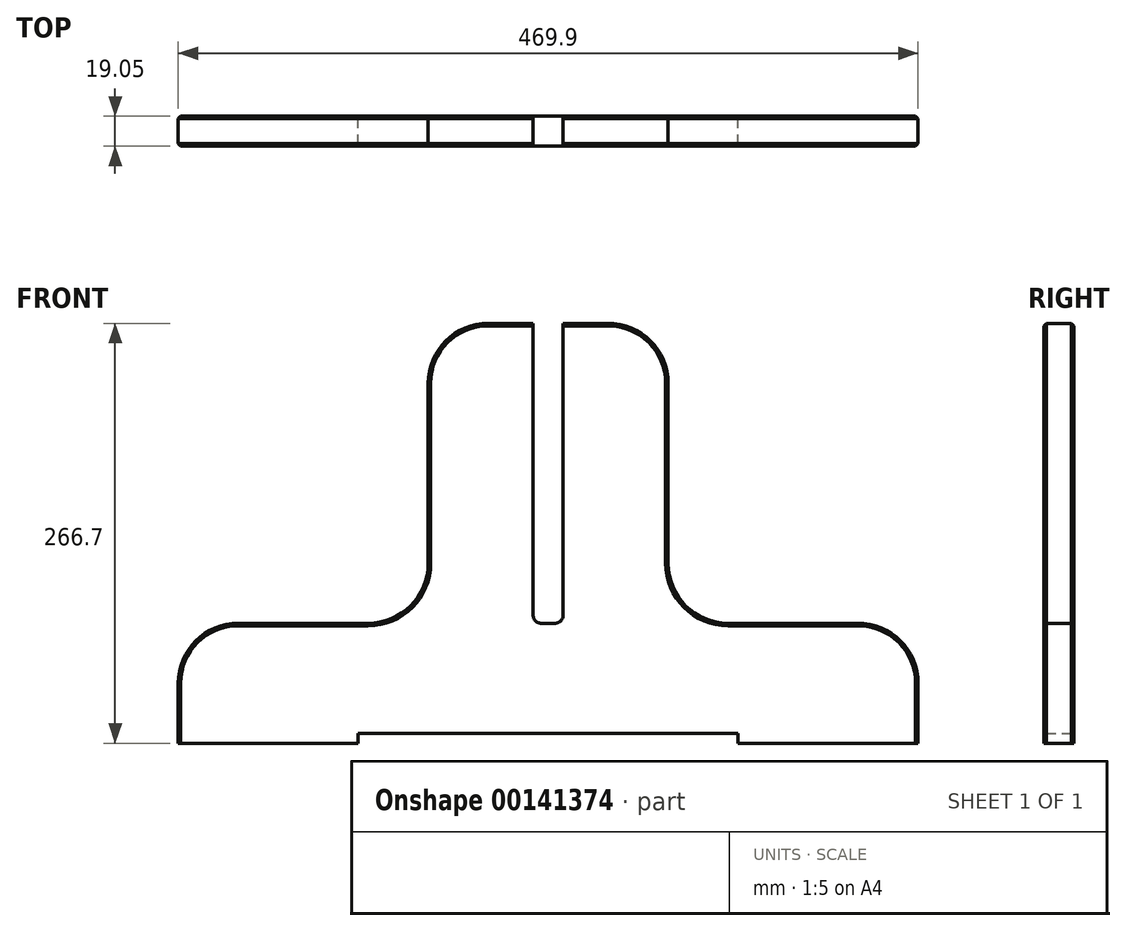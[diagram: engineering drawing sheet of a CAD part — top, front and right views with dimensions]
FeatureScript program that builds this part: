
annotation { "Feature Type Name" : "Feature", "Feature Type Description" : "" }
export const myFeature = defineFeature(function(context is Context, id is Id, definition is map)
    precondition{}
    {
        {
            var Q0;
            Q0=qCreatedBy(makeId("Front.planeOp"),FACE);
            var sketch = newSketch(context, id + "F0", { "sketchPlane" : qUnion([Q0])});
            skLineSegment(sketch, "E0.left", {"start": v(76.2, 95.25) * mm, "end": v(76.2, -95.25) * mm});
            skLineSegment(sketch, "E0.right", {"start": v(-76.2, 95.25) * mm, "end": v(-76.2, -95.25) * mm});
            skPoint(sketch, "E0.middle", {"position": v(0, 0) * mm});
            skLineSegment(sketch, "E1", {"start": v(-234.95, -171.45) * mm, "end": v(-234.95, -95.25) * mm});
            skLineSegment(sketch, "E2", {"start": v(-234.95, -95.25) * mm, "end": v(-76.2, -95.25) * mm});
            skLineSegment(sketch, "E3", {"start": v(234.95, -171.45) * mm, "end": v(234.95, -95.25) * mm});
            skLineSegment(sketch, "E4", {"start": v(234.95, -95.25) * mm, "end": v(76.2, -95.25) * mm});
            skLineSegment(sketch, "E5", {"start": v(-9.53, -95.25) * mm, "end": v(9.52, -95.25) * mm});
            skLineSegment(sketch, "E6", {"start": v(-76.2, 95.25) * mm, "end": v(-9.53, 95.25) * mm});
            skLineSegment(sketch, "E7", {"start": v(-9.53, 95.25) * mm, "end": v(-9.53, -95.25) * mm});
            skLineSegment(sketch, "E8", {"start": v(9.52, -95.25) * mm, "end": v(9.52, 95.25) * mm});
            skLineSegment(sketch, "E9", {"start": v(9.52, 95.25) * mm, "end": v(76.2, 95.25) * mm});
            skLineSegment(sketch, "E10", {"start": v(-234.95, -171.45) * mm, "end": v(-120.65, -171.45) * mm});
            skLineSegment(sketch, "E11", {"start": v(-120.65, -171.45) * mm, "end": v(-120.65, -165.1) * mm});
            skLineSegment(sketch, "E12", {"start": v(-120.65, -165.1) * mm, "end": v(120.65, -165.1) * mm});
            skLineSegment(sketch, "E13", {"start": v(120.65, -165.1) * mm, "end": v(120.65, -171.45) * mm});
            skLineSegment(sketch, "E14", {"start": v(120.65, -171.45) * mm, "end": v(234.95, -171.45) * mm});
            skSolve(sketch);
        }
        {
            var Q0;
            Q0=makeQuery(id+"F0.imprint","IMPRINT",FACE,{"disambiguationData":[TD([[makeQuery(id+"F0.imprint","IMPRINT",EDGE,{"derivedFrom":sQuery(id+"F0.wireOp",EDGE,"E0.left")}),-1.0]])]});
            extrude(context, id + "F1", {"entities" : qUnion([Q0]), "depth" : 19.05 * mm});
        }
        {
            var Q0;
            Q0=makeQuery(id+"F1.opExtrude","SWEPT_EDGE",EDGE,{"disambiguationData":[OSD([sQuery(id+"F0.wireOp",EDGE,"E1"),sQuery(id+"F0.wireOp",EDGE,"E2")])]});
            var Q1;
            Q1=makeQuery(id+"F1.opExtrude","SWEPT_EDGE",EDGE,{"disambiguationData":[OSD([sQuery(id+"F0.wireOp",EDGE,"E0.right"),sQuery(id+"F0.wireOp",EDGE,"E2")])]});
            var Q2;
            Q2=makeQuery(id+"F1.opExtrude","SWEPT_EDGE",EDGE,{"disambiguationData":[OSD([sQuery(id+"F0.wireOp",EDGE,"E0.left"),sQuery(id+"F0.wireOp",EDGE,"E4")])]});
            var Q3;
            Q3=makeQuery(id+"F1.opExtrude","SWEPT_EDGE",EDGE,{"disambiguationData":[OSD([sQuery(id+"F0.wireOp",EDGE,"E3"),sQuery(id+"F0.wireOp",EDGE,"E4")])]});
            var Q4;
            Q4=makeQuery(id+"F1.opExtrude","SWEPT_EDGE",EDGE,{"disambiguationData":[OSD([sQuery(id+"F0.wireOp",EDGE,"E0.left"),sQuery(id+"F0.wireOp",EDGE,"E9")])]});
            var Q5;
            Q5=makeQuery(id+"F1.opExtrude","SWEPT_EDGE",EDGE,{"disambiguationData":[OSD([sQuery(id+"F0.wireOp",EDGE,"E0.right"),sQuery(id+"F0.wireOp",EDGE,"E6")])]});
            fillet(context, id + "F2", {"entities" : qUnion([Q0, Q1, Q2, Q3, Q4, Q5]), "radius" : 38.1 * mm, "tangentPropagation" : true, "allowEdgeOverflow" : false});
        }
        {
            var Q0;
            Q0=makeQuery(id+"F1.opExtrude","SWEPT_EDGE",EDGE,{"disambiguationData":[OSD([sQuery(id+"F0.wireOp",EDGE,"E5"),sQuery(id+"F0.wireOp",EDGE,"E8")])]});
            var Q1;
            Q1=makeQuery(id+"F1.opExtrude","SWEPT_EDGE",EDGE,{"disambiguationData":[OSD([sQuery(id+"F0.wireOp",EDGE,"E5"),sQuery(id+"F0.wireOp",EDGE,"E7")])]});
            fillet(context, id + "F3", {"entities" : qUnion([Q0, Q1]), "radius" : 5.08 * mm, "tangentPropagation" : true, "allowEdgeOverflow" : false});
        }
        {
            var Q0;
            Q0=makeQuery(id+"F1.opExtrude","CAP_EDGE",EDGE,{"disambiguationData":[OSD([sQuery(id+"F0.wireOp",EDGE,"E2")])],"isStart":false});
            var Q1;
            Q1=makeQuery(id+"F1.opExtrude","CAP_EDGE",EDGE,{"disambiguationData":[OSD([sQuery(id+"F0.wireOp",EDGE,"E4")])],"isStart":false});
            var Q2;
            Q2=makeQuery(id+"F1.opExtrude","CAP_EDGE",EDGE,{"disambiguationData":[OSD([sQuery(id+"F0.wireOp",EDGE,"E4")])],"isStart":true});
            var Q3;
            Q3=makeQuery(id+"F1.opExtrude","CAP_EDGE",EDGE,{"disambiguationData":[OSD([sQuery(id+"F0.wireOp",EDGE,"E6")])],"isStart":true});
            chamfer(context, id + "F4", {"entities" : qUnion([Q0, Q1, Q2, Q3]), "width" : 1.59 * mm, "tangentPropagation" : true});
        }
    });
